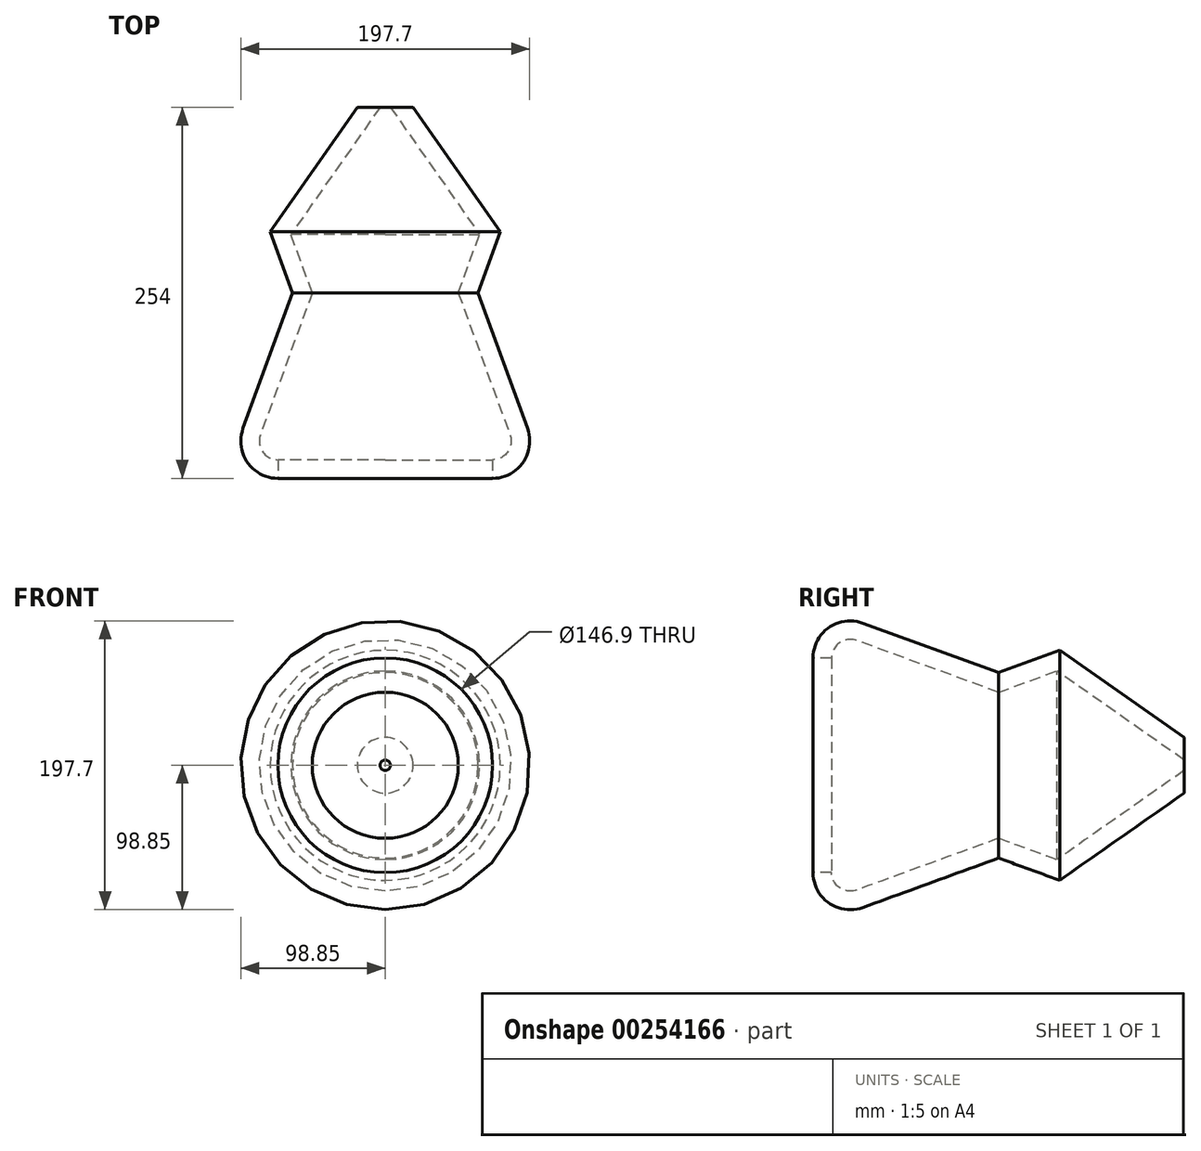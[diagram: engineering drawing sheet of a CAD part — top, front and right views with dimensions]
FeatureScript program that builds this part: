
annotation { "Feature Type Name" : "Feature", "Feature Type Description" : "" }
export const myFeature = defineFeature(function(context is Context, id is Id, definition is map)
    precondition{}
    {
        {
            var Q0;
            Q0=qCreatedBy(makeId("Front.planeOp"),FACE);
            var sketch = newSketch(context, id + "F0", { "sketchPlane" : qUnion([Q0])});
            skCircle(sketch, "E0", {"center": v(0, 0) * mm, "radius": 63.5 * mm});
            skSolve(sketch);
        }
        {
            var Q0;
            Q0=makeQuery(id+"F0.imprint","IMPRINT",FACE,{"disambiguationData":[TD([[makeQuery(id+"F0.imprint","IMPRINT",EDGE,{"derivedFrom":sQuery(id+"F0.wireOp",EDGE,"E0")}),1.0]])]});
            extrude(context, id + "F1", {"entities" : qUnion([Q0]), "endBound" : BoundingType.SYMMETRIC, "depth" : 254 * mm, "hasDraft" : true, "draftAngle" : 20 * degree});
        }
        {
            var Q0;
            Q0=makeQuery(id+"F1.opExtrude","CAP_EDGE",EDGE,{"disambiguationData":[OSD([sQuery(id+"F0.wireOp",EDGE,"E0")])],"isStart":false});
            fillet(context, id + "F2", {"entities" : qUnion([Q0]), "radius" : 25.4 * mm, "tangentPropagation" : true, "allowEdgeOverflow" : false});
        }
        {
            var Q0;
            Q0=makeQuery(id+"F1.opExtrude","CAP_EDGE",EDGE,{"disambiguationData":[OSD([sQuery(id+"F0.wireOp",EDGE,"E0")])],"isStart":true});
            chamfer(context, id + "F3", {"entities" : qUnion([Q0]), "width" : 63.5 * mm, "tangentPropagation" : true});
        }
        {
            var Q0;
            Q0=makeQuery(id+"F1.opExtrude","CAP_FACE",FACE,{"disambiguationData":[OSD([sQuery(id+"F0.wireOp",EDGE,"E0")])],"isStart":false});
            var Q1;
            Q1=makeQuery(id+"F1.opExtrude","CAP_FACE",FACE,{"disambiguationData":[OSD([sQuery(id+"F0.wireOp",EDGE,"E0")])],"isStart":true});
            shell(context, id + "F4", {"entities" : qUnion([Q0, Q1]), "thickness" : 12.7 * mm});
        }
    });
